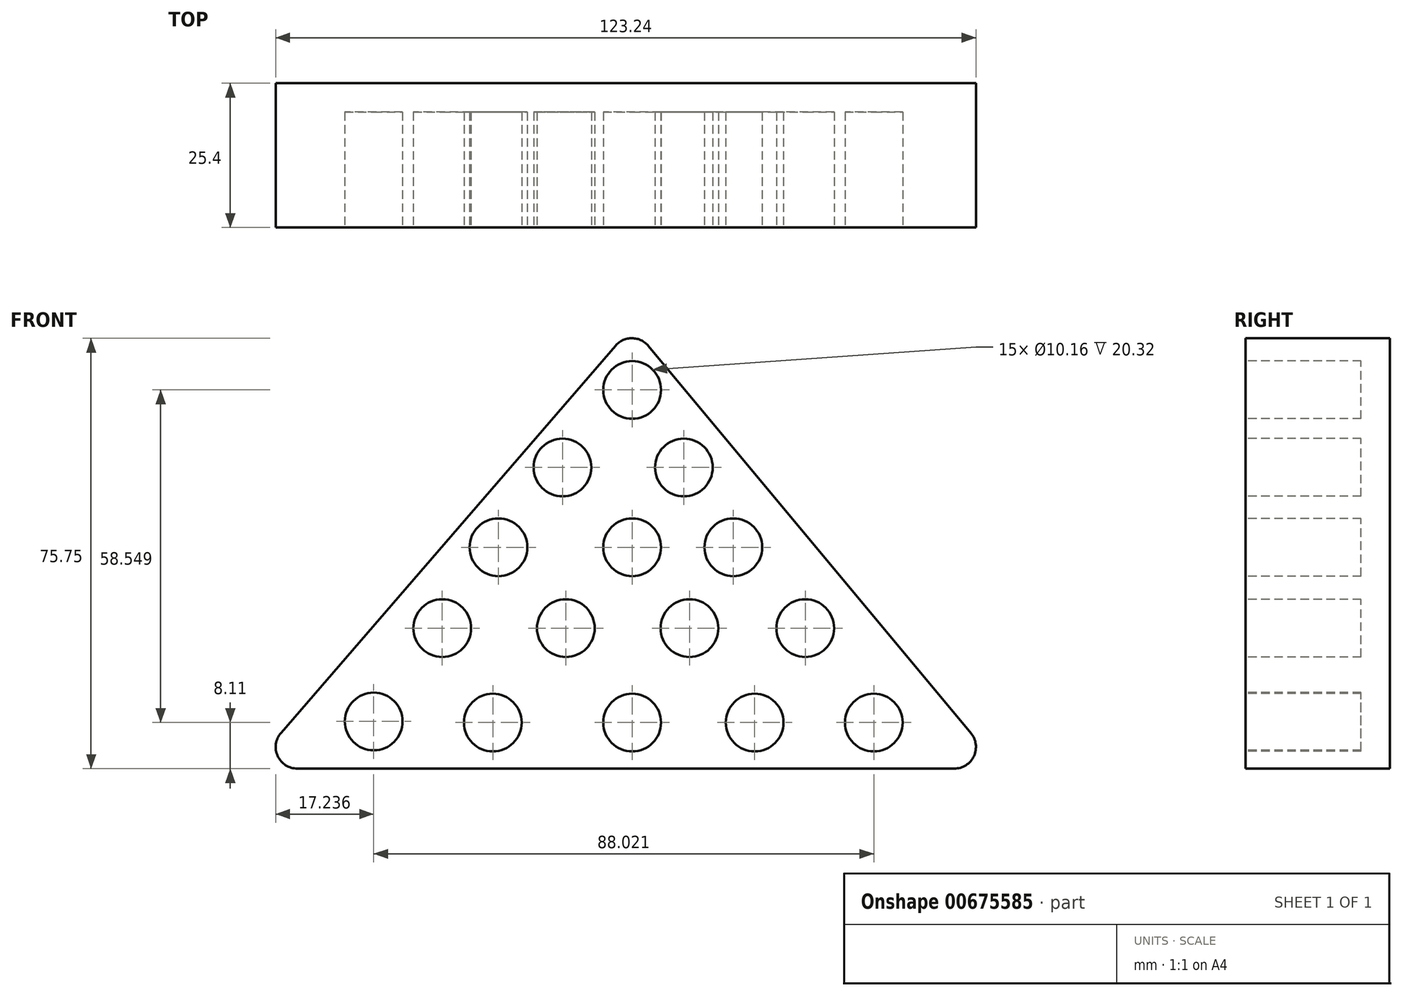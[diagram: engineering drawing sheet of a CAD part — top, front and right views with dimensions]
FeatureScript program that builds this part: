
annotation { "Feature Type Name" : "Feature", "Feature Type Description" : "" }
export const myFeature = defineFeature(function(context is Context, id is Id, definition is map)
    precondition{}
    {
        {
            var Q0;
            Q0=qCreatedBy(makeId("Front.planeOp"),FACE);
            var sketch = newSketch(context, id + "F0", { "sketchPlane" : qUnion([Q0])});
            skLineSegment(sketch, "E0", {"start": v(-2.94, 74.44) * mm, "end": v(-61.8, 6.3) * mm});
            skLineSegment(sketch, "E1", {"start": v(2.87, 74.38) * mm, "end": v(59.62, 6.25) * mm});
            skLineSegment(sketch, "E2", {"start": v(56.7, 0) * mm, "end": v(-58.92, 0) * mm});
            skPoint(sketch, "E3.visualSharp", {"position": v(0, 77.83) * mm});
            skArc(sketch, "E3.filletArc", {"start": v(2.87, 74.38) * mm, "mid": v(-0.02, 75.75) * mm, "end": v(-2.94, 74.44) * mm});
            skPoint(sketch, "E4.visualSharp", {"position": v(-67.25, 0) * mm});
            skArc(sketch, "E4.filletArc", {"start": v(-61.8, 6.3) * mm, "mid": v(-62.39, 2.22) * mm, "end": v(-58.92, 0) * mm});
            skPoint(sketch, "E5.visualSharp", {"position": v(64.83, 0) * mm});
            skArc(sketch, "E5.filletArc", {"start": v(56.7, 0) * mm, "mid": v(60.15, 2.2) * mm, "end": v(59.62, 6.25) * mm});
            skSolve(sketch);
        }
        {
            var Q0;
            Q0 = qSketchRegion(id + "F0", true);
            extrude(context, id + "F1", {"entities" : qUnion([Q0]), "depth" : 25.4 * mm, "offsetDistance" : 25.4 * mm});
        }
        {
            var Q0;
            Q0=makeQuery(id+"F1.opExtrude","CAP_FACE",FACE,{"disambiguationData":[OSD([sQuery(id+"F0.wireOp",EDGE,"E0"),sQuery(id+"F0.wireOp",EDGE,"E1"),sQuery(id+"F0.wireOp",EDGE,"E2"),sQuery(id+"F0.wireOp",EDGE,"E3.filletArc"),sQuery(id+"F0.wireOp",EDGE,"E4.filletArc"),sQuery(id+"F0.wireOp",EDGE,"E5.filletArc")])],"isStart":false});
            var sketch = newSketch(context, id + "F2", { "sketchPlane" : qUnion([Q0])});
            skCircle(sketch, "E6", {"center": v(0, 66.66) * mm, "radius": 5.08 * mm});
            skCircle(sketch, "E7", {"center": v(-12.26, 53.01) * mm, "radius": 5.08 * mm});
            skCircle(sketch, "E8", {"center": v(9.1, 53.01) * mm, "radius": 5.08 * mm});
            skCircle(sketch, "E9", {"center": v(-45.5, 8.3) * mm, "radius": 5.08 * mm});
            skCircle(sketch, "E10", {"center": v(-24.53, 8.1) * mm, "radius": 5.08 * mm});
            skCircle(sketch, "E11", {"center": v(0, 8.1) * mm, "radius": 5.08 * mm});
            skCircle(sketch, "E12", {"center": v(21.56, 8.1) * mm, "radius": 5.08 * mm});
            skCircle(sketch, "E13", {"center": v(42.53, 8.1) * mm, "radius": 5.08 * mm});
            skCircle(sketch, "E14", {"center": v(-33.43, 24.72) * mm, "radius": 5.08 * mm});
            skCircle(sketch, "E15", {"center": v(-11.67, 24.72) * mm, "radius": 5.08 * mm});
            skCircle(sketch, "E16", {"center": v(10.09, 24.72) * mm, "radius": 5.08 * mm});
            skCircle(sketch, "E17", {"center": v(30.46, 24.72) * mm, "radius": 5.08 * mm});
            skCircle(sketch, "E18", {"center": v(-23.54, 38.97) * mm, "radius": 5.08 * mm});
            skCircle(sketch, "E19", {"center": v(0, 38.97) * mm, "radius": 5.08 * mm});
            skCircle(sketch, "E20", {"center": v(17.8, 38.97) * mm, "radius": 5.08 * mm});
            skSolve(sketch);
        }
        {
            var Q0;
            Q0=makeQuery(id+"F2.imprint","IMPRINT",FACE,{"disambiguationData":[TD([[makeQuery(id+"F2.imprint","IMPRINT",EDGE,{"derivedFrom":sQuery(id+"F2.wireOp",EDGE,"E9")}),1.0]])]});
            var Q1;
            Q1=makeQuery(id+"F2.imprint","IMPRINT",FACE,{"disambiguationData":[TD([[makeQuery(id+"F2.imprint","IMPRINT",EDGE,{"derivedFrom":sQuery(id+"F2.wireOp",EDGE,"E10")}),1.0]])]});
            var Q2;
            Q2=makeQuery(id+"F2.imprint","IMPRINT",FACE,{"disambiguationData":[TD([[makeQuery(id+"F2.imprint","IMPRINT",EDGE,{"derivedFrom":sQuery(id+"F2.wireOp",EDGE,"E14")}),1.0]])]});
            var Q3;
            Q3=makeQuery(id+"F2.imprint","IMPRINT",FACE,{"disambiguationData":[TD([[makeQuery(id+"F2.imprint","IMPRINT",EDGE,{"derivedFrom":sQuery(id+"F2.wireOp",EDGE,"E15")}),1.0]])]});
            var Q4;
            Q4=makeQuery(id+"F2.imprint","IMPRINT",FACE,{"disambiguationData":[TD([[makeQuery(id+"F2.imprint","IMPRINT",EDGE,{"derivedFrom":sQuery(id+"F2.wireOp",EDGE,"E11")}),1.0]])]});
            var Q5;
            Q5=makeQuery(id+"F2.imprint","IMPRINT",FACE,{"disambiguationData":[TD([[makeQuery(id+"F2.imprint","IMPRINT",EDGE,{"derivedFrom":sQuery(id+"F2.wireOp",EDGE,"E12")}),1.0]])]});
            var Q6;
            Q6=makeQuery(id+"F2.imprint","IMPRINT",FACE,{"disambiguationData":[TD([[makeQuery(id+"F2.imprint","IMPRINT",EDGE,{"derivedFrom":sQuery(id+"F2.wireOp",EDGE,"E13")}),1.0]])]});
            var Q7;
            Q7=makeQuery(id+"F2.imprint","IMPRINT",FACE,{"disambiguationData":[TD([[makeQuery(id+"F2.imprint","IMPRINT",EDGE,{"derivedFrom":sQuery(id+"F2.wireOp",EDGE,"E17")}),1.0]])]});
            var Q8;
            Q8=makeQuery(id+"F2.imprint","IMPRINT",FACE,{"disambiguationData":[TD([[makeQuery(id+"F2.imprint","IMPRINT",EDGE,{"derivedFrom":sQuery(id+"F2.wireOp",EDGE,"E16")}),1.0]])]});
            var Q9;
            Q9=makeQuery(id+"F2.imprint","IMPRINT",FACE,{"disambiguationData":[TD([[makeQuery(id+"F2.imprint","IMPRINT",EDGE,{"derivedFrom":sQuery(id+"F2.wireOp",EDGE,"E19")}),1.0]])]});
            var Q10;
            Q10=makeQuery(id+"F2.imprint","IMPRINT",FACE,{"disambiguationData":[TD([[makeQuery(id+"F2.imprint","IMPRINT",EDGE,{"derivedFrom":sQuery(id+"F2.wireOp",EDGE,"E18")}),1.0]])]});
            var Q11;
            Q11=makeQuery(id+"F2.imprint","IMPRINT",FACE,{"disambiguationData":[TD([[makeQuery(id+"F2.imprint","IMPRINT",EDGE,{"derivedFrom":sQuery(id+"F2.wireOp",EDGE,"E6")}),1.0]])]});
            var Q12;
            Q12=makeQuery(id+"F2.imprint","IMPRINT",FACE,{"disambiguationData":[TD([[makeQuery(id+"F2.imprint","IMPRINT",EDGE,{"derivedFrom":sQuery(id+"F2.wireOp",EDGE,"E7")}),1.0]])]});
            var Q13;
            Q13=makeQuery(id+"F2.imprint","IMPRINT",FACE,{"disambiguationData":[TD([[makeQuery(id+"F2.imprint","IMPRINT",EDGE,{"derivedFrom":sQuery(id+"F2.wireOp",EDGE,"E8")}),1.0]])]});
            var Q14;
            Q14=makeQuery(id+"F2.imprint","IMPRINT",FACE,{"disambiguationData":[TD([[makeQuery(id+"F2.imprint","IMPRINT",EDGE,{"derivedFrom":sQuery(id+"F2.wireOp",EDGE,"E20")}),1.0]])]});
            extrude(context, id + "F3", {"entities" : qUnion([Q0, Q1, Q2, Q3, Q4, Q5, Q6, Q7, Q8, Q9, Q10, Q11, Q12, Q13, Q14]), "operationType" : NewBodyOperationType.REMOVE, "oppositeDirection" : true, "depth" : 20.32 * mm, "offsetDistance" : 25.4 * mm});
        }
    });
